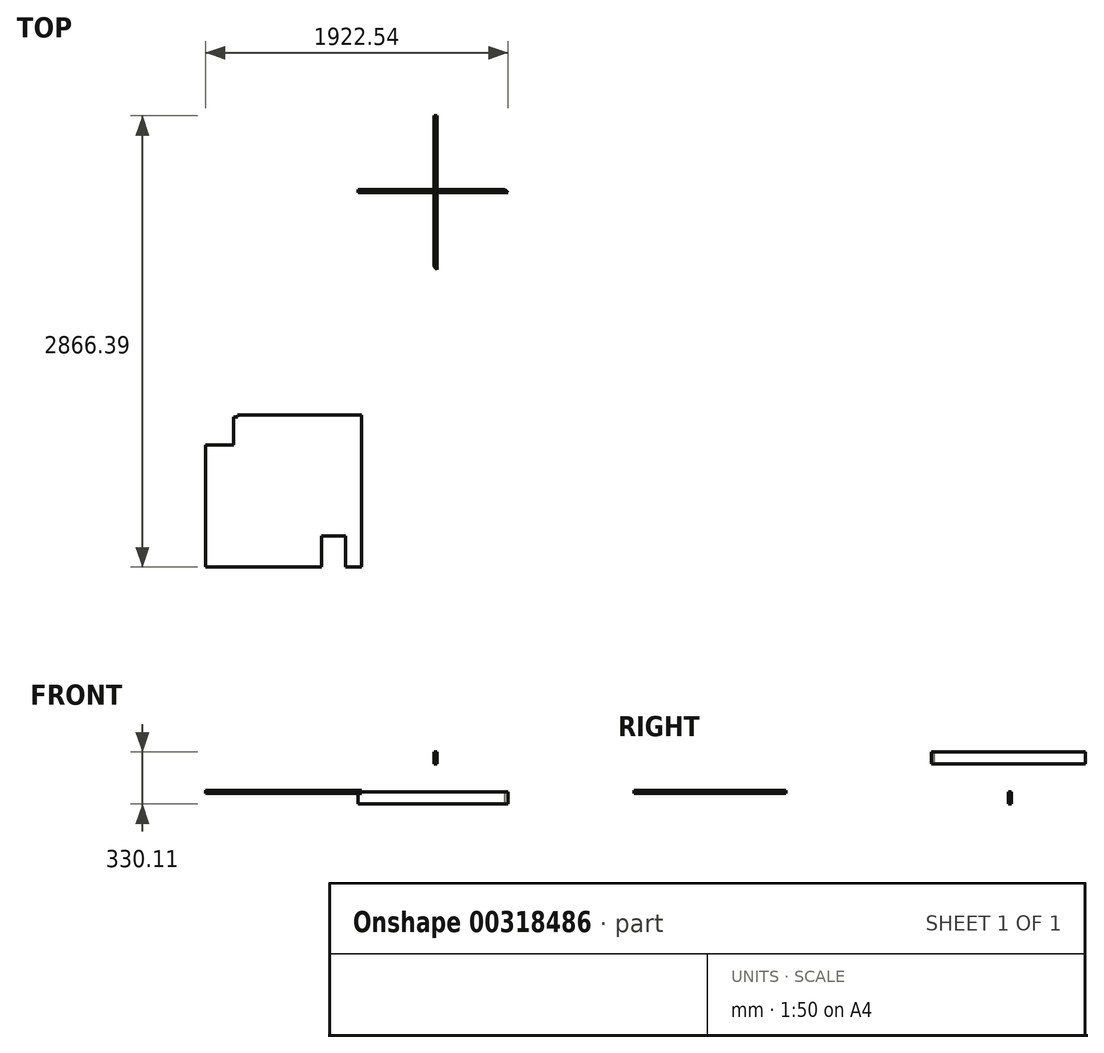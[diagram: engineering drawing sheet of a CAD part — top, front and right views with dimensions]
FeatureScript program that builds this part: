
annotation { "Feature Type Name" : "Feature", "Feature Type Description" : "" }
export const myFeature = defineFeature(function(context is Context, id is Id, definition is map)
    precondition{}
    {
        {
            var Q0;
            Q0=qCreatedBy(makeId("Front.planeOp"),FACE);
            var sketch = newSketch(context, id + "F0", { "sketchPlane" : qUnion([Q0])});
            skLineSegment(sketch, "E0.bottom", {"start": v(-482.07, 7.55) * mm, "end": v(470.43, 7.55) * mm});
            skLineSegment(sketch, "E0.top", {"start": v(-482.07, -68.65) * mm, "end": v(470.43, -68.65) * mm});
            skLineSegment(sketch, "E0.left", {"start": v(-482.07, 7.55) * mm, "end": v(-482.07, -68.65) * mm});
            skLineSegment(sketch, "E0.right", {"start": v(470.43, 7.55) * mm, "end": v(470.43, -68.65) * mm});
            skSolve(sketch);
        }
        {
            var Q0;
            Q0 = qSketchRegion(id + "F0", true);
            extrude(context, id + "F1", {"entities" : qUnion([Q0]), "depth" : 19.05 * mm});
        }
        {
            var Q0;
            Q0=makeQuery(id+"F1.opExtrude","SWEPT_FACE",FACE,{"disambiguationData":[OSD([sQuery(id+"F0.wireOp",EDGE,"E0.bottom")])]});
            var sketch = newSketch(context, id + "F2", { "sketchPlane" : qUnion([Q0])});
            skLineSegment(sketch, "E1.0", {"start": v(451.38, -19.05) * mm, "end": v(451.38, 0) * mm, "construction": true});
            skLineSegment(sketch, "E2", {"start": v(470.43, -19.05) * mm, "end": v(451.38, 0) * mm});
            skSolve(sketch);
        }
        {
            var Q0;
            {var subQ0=sQuery(id+"F2.wireOp",EDGE,"E2");Q0=makeQuery(id+"F2.imprint","IMPRINT",FACE,{"disambiguationData":[TD([[makeQuery(id+"F2.imprint","IMPRINT",EDGE,{"derivedFrom":subQ0}),-1.0]])]});}
            extrude(context, id + "F3", {"entities" : qUnion([Q0]), "operationType" : NewBodyOperationType.REMOVE, "oppositeDirection" : true, "depth" : 76.2 * mm});
        }
        {
            var Q0;
            Q0=qCreatedBy(makeId("Right.planeOp"),FACE);
            var sketch = newSketch(context, id + "F4", { "sketchPlane" : qUnion([Q0])});
            skLineSegment(sketch, "E3.bottom", {"start": v(-508.83, 261.46) * mm, "end": v(469.07, 261.46) * mm});
            skLineSegment(sketch, "E3.top", {"start": v(-508.83, 185.26) * mm, "end": v(469.07, 185.26) * mm});
            skLineSegment(sketch, "E3.left", {"start": v(-508.83, 261.46) * mm, "end": v(-508.83, 185.26) * mm});
            skLineSegment(sketch, "E3.right", {"start": v(469.07, 261.46) * mm, "end": v(469.07, 185.26) * mm});
            skSolve(sketch);
        }
        {
            var Q0;
            Q0=makeQuery(id+"F4.imprint","IMPRINT",FACE,{"disambiguationData":[TD([[makeQuery(id+"F4.imprint","IMPRINT",EDGE,{"derivedFrom":sQuery(id+"F4.wireOp",EDGE,"E3.bottom")}),-1.0]])]});
            extrude(context, id + "F5", {"entities" : qUnion([Q0]), "depth" : 19.05 * mm});
        }
        {
            var Q0;
            Q0=makeQuery(id+"F5.opExtrude","SWEPT_FACE",FACE,{"disambiguationData":[OSD([sQuery(id+"F4.wireOp",EDGE,"E3.bottom")])]});
            var sketch = newSketch(context, id + "F6", { "sketchPlane" : qUnion([Q0])});
            skLineSegment(sketch, "E4.0", {"start": v(19.05, -489.78) * mm, "end": v(0, -489.78) * mm, "construction": true});
            skLineSegment(sketch, "E5", {"start": v(19.05, -508.83) * mm, "end": v(0, -489.78) * mm});
            skSolve(sketch);
        }
        {
            var Q0;
            {var subQ0=sQuery(id+"F6.wireOp",EDGE,"E5");Q0=makeQuery(id+"F6.imprint","IMPRINT",FACE,{"disambiguationData":[TD([[makeQuery(id+"F6.imprint","IMPRINT",EDGE,{"derivedFrom":subQ0}),1.0]])]});}
            extrude(context, id + "F7", {"entities" : qUnion([Q0]), "operationType" : NewBodyOperationType.REMOVE, "oppositeDirection" : true, "depth" : 76.2 * mm});
        }
        {
            var Q0;
            Q0=qCreatedBy(makeId("Top.planeOp"),FACE);
            var sketch = newSketch(context, id + "F8", { "sketchPlane" : qUnion([Q0])});
            skLineSegment(sketch, "E6.bottom", {"start": v(-1452.11, -2397.32) * mm, "end": v(-715.51, -2397.32) * mm});
            skLineSegment(sketch, "E6.top", {"start": v(-1248.91, -1432.12) * mm, "end": v(-461.51, -1432.12) * mm});
            skLineSegment(sketch, "E6.left", {"start": v(-1452.11, -2397.32) * mm, "end": v(-1452.11, -1622.62) * mm});
            skLineSegment(sketch, "E6.right", {"start": v(-461.51, -2397.32) * mm, "end": v(-461.51, -1432.12) * mm});
            skLineSegment(sketch, "E7", {"start": v(-1452.11, -1622.62) * mm, "end": v(-1274.31, -1622.62) * mm});
            skLineSegment(sketch, "E8", {"start": v(-1274.31, -1622.62) * mm, "end": v(-1274.31, -1444.82) * mm});
            skLineSegment(sketch, "E9", {"start": v(-715.51, -2397.32) * mm, "end": v(-715.51, -2200.47) * mm});
            skLineSegment(sketch, "E10", {"start": v(-715.51, -2200.47) * mm, "end": v(-563.11, -2200.47) * mm});
            skLineSegment(sketch, "E11", {"start": v(-563.11, -2200.47) * mm, "end": v(-563.11, -2397.32) * mm});
            skLineSegment(sketch, "E12", {"start": v(-1274.31, -1444.82) * mm, "end": v(-1248.91, -1444.82) * mm});
            skLineSegment(sketch, "E13", {"start": v(-1248.91, -1444.82) * mm, "end": v(-1248.91, -1432.12) * mm});
            skLineSegment(sketch, "E14.trimOffspring", {"start": v(-563.11, -2397.32) * mm, "end": v(-461.51, -2397.32) * mm});
            skSolve(sketch);
        }
        {
            var Q0;
            Q0 = qSketchRegion(id + "F8", true);
            extrude(context, id + "F9", {"entities" : qUnion([Q0]), "depth" : 19.05 * mm});
        }
    });
